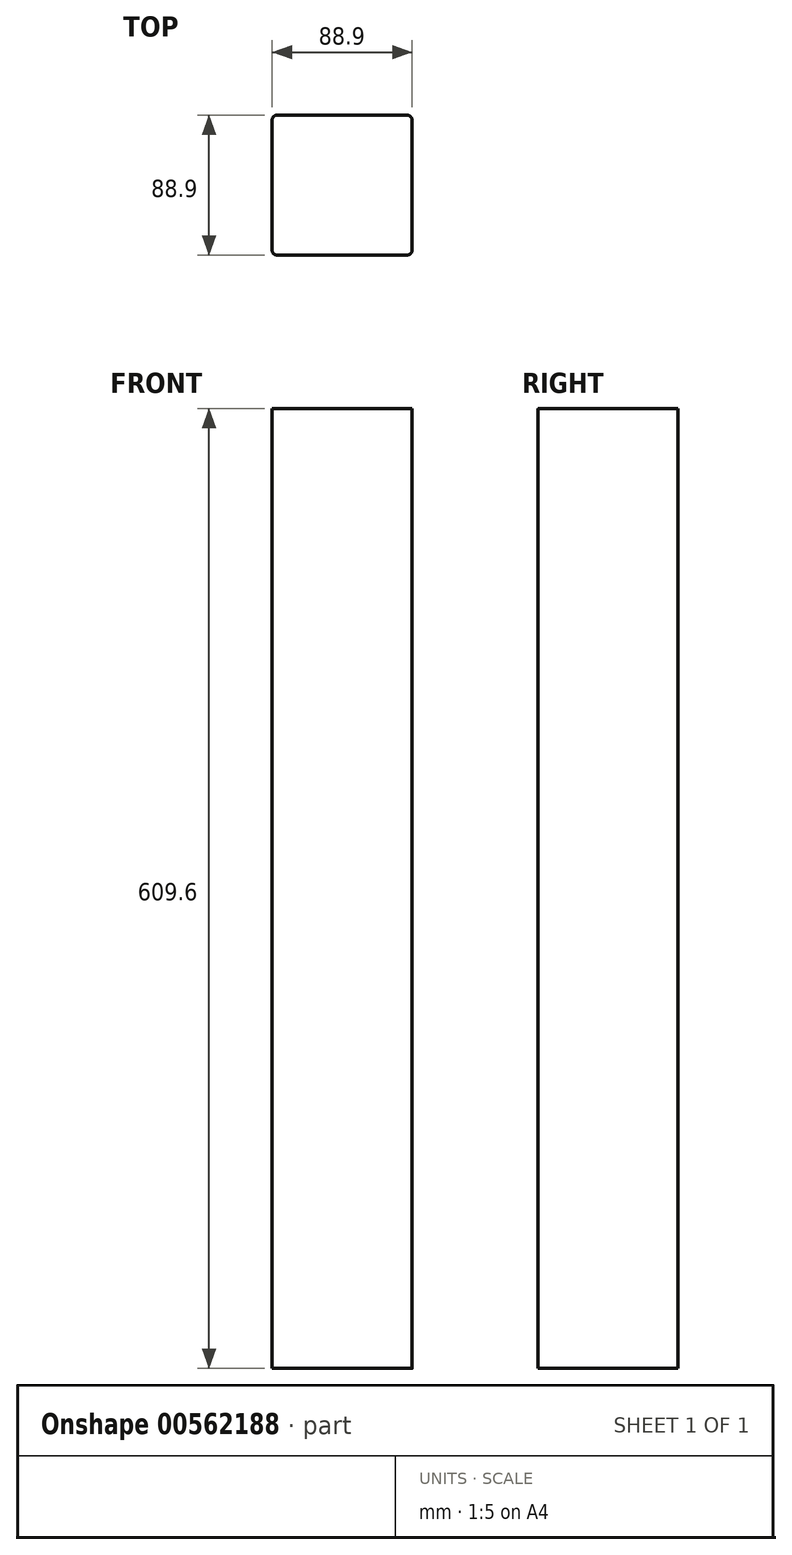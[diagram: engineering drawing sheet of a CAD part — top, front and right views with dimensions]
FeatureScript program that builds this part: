
annotation { "Feature Type Name" : "Feature", "Feature Type Description" : "" }
export const myFeature = defineFeature(function(context is Context, id is Id, definition is map)
    precondition{}
    {
        {
            var Q0;
            Q0=qCreatedBy(makeId("Top.planeOp"),FACE);
            var sketch = newSketch(context, id + "F0", { "sketchPlane" : qUnion([Q0])});
            skLineSegment(sketch, "E0.bottom", {"start": v(-41.28, 44.45) * mm, "end": v(41.28, 44.45) * mm});
            skLineSegment(sketch, "E0.top", {"start": v(-41.28, -44.45) * mm, "end": v(41.27, -44.45) * mm});
            skLineSegment(sketch, "E0.left", {"start": v(-44.45, 41.28) * mm, "end": v(-44.45, -41.28) * mm});
            skLineSegment(sketch, "E0.right", {"start": v(44.45, 41.28) * mm, "end": v(44.45, -41.28) * mm});
            skLineSegment(sketch, "E1", {"start": v(0, 0) * mm, "end": v(0, 44.45) * mm, "construction": true});
            skLineSegment(sketch, "E2", {"start": v(0, 0) * mm, "end": v(44.45, 0) * mm, "construction": true});
            skPoint(sketch, "E3.visualSharp", {"position": v(-44.45, -44.45) * mm});
            skArc(sketch, "E3.filletArc", {"start": v(-44.45, -41.28) * mm, "mid": v(-43.52, -43.52) * mm, "end": v(-41.28, -44.45) * mm});
            skPoint(sketch, "E4.visualSharp", {"position": v(44.45, -44.45) * mm});
            skArc(sketch, "E4.filletArc", {"start": v(41.27, -44.45) * mm, "mid": v(43.52, -43.52) * mm, "end": v(44.45, -41.28) * mm});
            skPoint(sketch, "E5.visualSharp", {"position": v(44.45, 44.45) * mm});
            skArc(sketch, "E5.filletArc", {"start": v(44.45, 41.28) * mm, "mid": v(43.52, 43.52) * mm, "end": v(41.28, 44.45) * mm});
            skPoint(sketch, "E6.visualSharp", {"position": v(-44.45, 44.45) * mm});
            skArc(sketch, "E6.filletArc", {"start": v(-41.28, 44.45) * mm, "mid": v(-43.52, 43.52) * mm, "end": v(-44.45, 41.28) * mm});
            skSolve(sketch);
        }
        {
            var Q0;
            Q0=makeQuery(id+"F0.imprint","IMPRINT",FACE,{"disambiguationData":[TD([[makeQuery(id+"F0.imprint","IMPRINT",EDGE,{"derivedFrom":sQuery(id+"F0.wireOp",EDGE,"E0.bottom")}),-1.0]])]});
            extrude(context, id + "F1", {"entities" : qUnion([Q0]), "depth" : 609.6 * mm, "offsetDistance" : 25.4 * mm});
        }
    });
